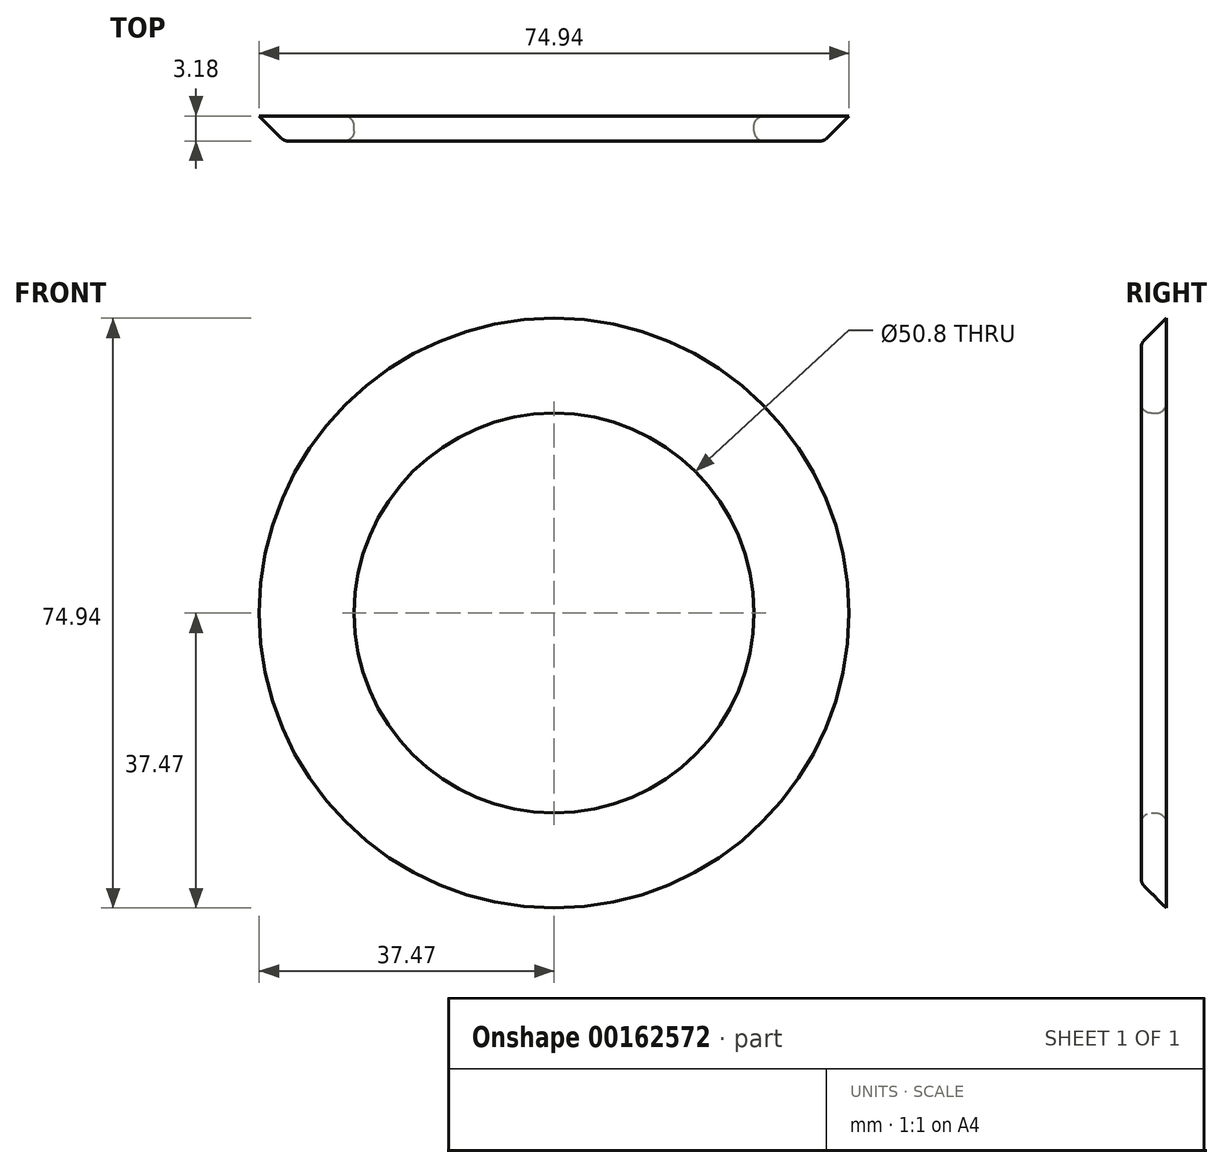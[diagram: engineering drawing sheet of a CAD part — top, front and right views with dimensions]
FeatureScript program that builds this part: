
annotation { "Feature Type Name" : "Feature", "Feature Type Description" : "" }
export const myFeature = defineFeature(function(context is Context, id is Id, definition is map)
    precondition{}
    {
        {
            var Q0;
            Q0=qCreatedBy(makeId("Front.planeOp"),FACE);
            var sketch = newSketch(context, id + "F0", { "sketchPlane" : qUnion([Q0])});
            skCircle(sketch, "E0", {"center": v(0, 0) * mm, "radius": 25.4 * mm});
            skCircle(sketch, "E1", {"center": v(0, 0) * mm, "radius": 38.1 * mm});
            skSolve(sketch);
        }
        {
            var Q0;
            Q0 = qSketchRegion(id + "F0", true);
            extrude(context, id + "F1", {"entities" : qUnion([Q0]), "depth" : 3.17 * mm});
        }
        {
            var Q0;
            Q0=makeQuery(id+"F1.opExtrude","CAP_EDGE",EDGE,{"disambiguationData":[OSD([sQuery(id+"F0.wireOp",EDGE,"E0")])],"isStart":true});
            var Q1;
            Q1=makeQuery(id+"F1.opExtrude","CAP_EDGE",EDGE,{"disambiguationData":[OSD([sQuery(id+"F0.wireOp",EDGE,"E0")])],"isStart":false});
            fillet(context, id + "F2", {"entities" : qUnion([Q0, Q1]), "radius" : 1.27 * mm, "tangentPropagation" : true, "allowEdgeOverflow" : false});
        }
        {
            var Q0;
            Q0=makeQuery(id+"F1.opExtrude","CAP_EDGE",EDGE,{"disambiguationData":[OSD([sQuery(id+"F0.wireOp",EDGE,"E1")])],"isStart":false});
            chamfer(context, id + "F4", {"entities" : qUnion([Q0]), "width" : 3.8 * mm, "tangentPropagation" : true});
        }
        {
            var Q0;
            {var subQ0=sQuery(id+"F0.wireOp",EDGE,"E1");Q0=makeQuery(id+"F4.opChamfer","BLEND_EDGE",EDGE,{"blendedFrom":[makeQuery(id+"F1.opExtrude","CAP_EDGE",EDGE,{"disambiguationData":[OSD([subQ0])],"isStart":false}),makeQuery(id+"F1.opExtrude","CAP_FACE",FACE,{"disambiguationData":[OSD([sQuery(id+"F0.wireOp",EDGE,"E0"),subQ0])],"isStart":false})],"blendedInto":[makeQuery(id+"F1.opExtrude","CAP_FACE",FACE,{"disambiguationData":[OSD([sQuery(id+"F0.wireOp",EDGE,"E0"),subQ0])],"isStart":false})]});}
            fillet(context, id + "F3", {"entities" : qUnion([Q0]), "radius" : 1.27 * mm, "tangentPropagation" : true, "allowEdgeOverflow" : false});
        }
    });
